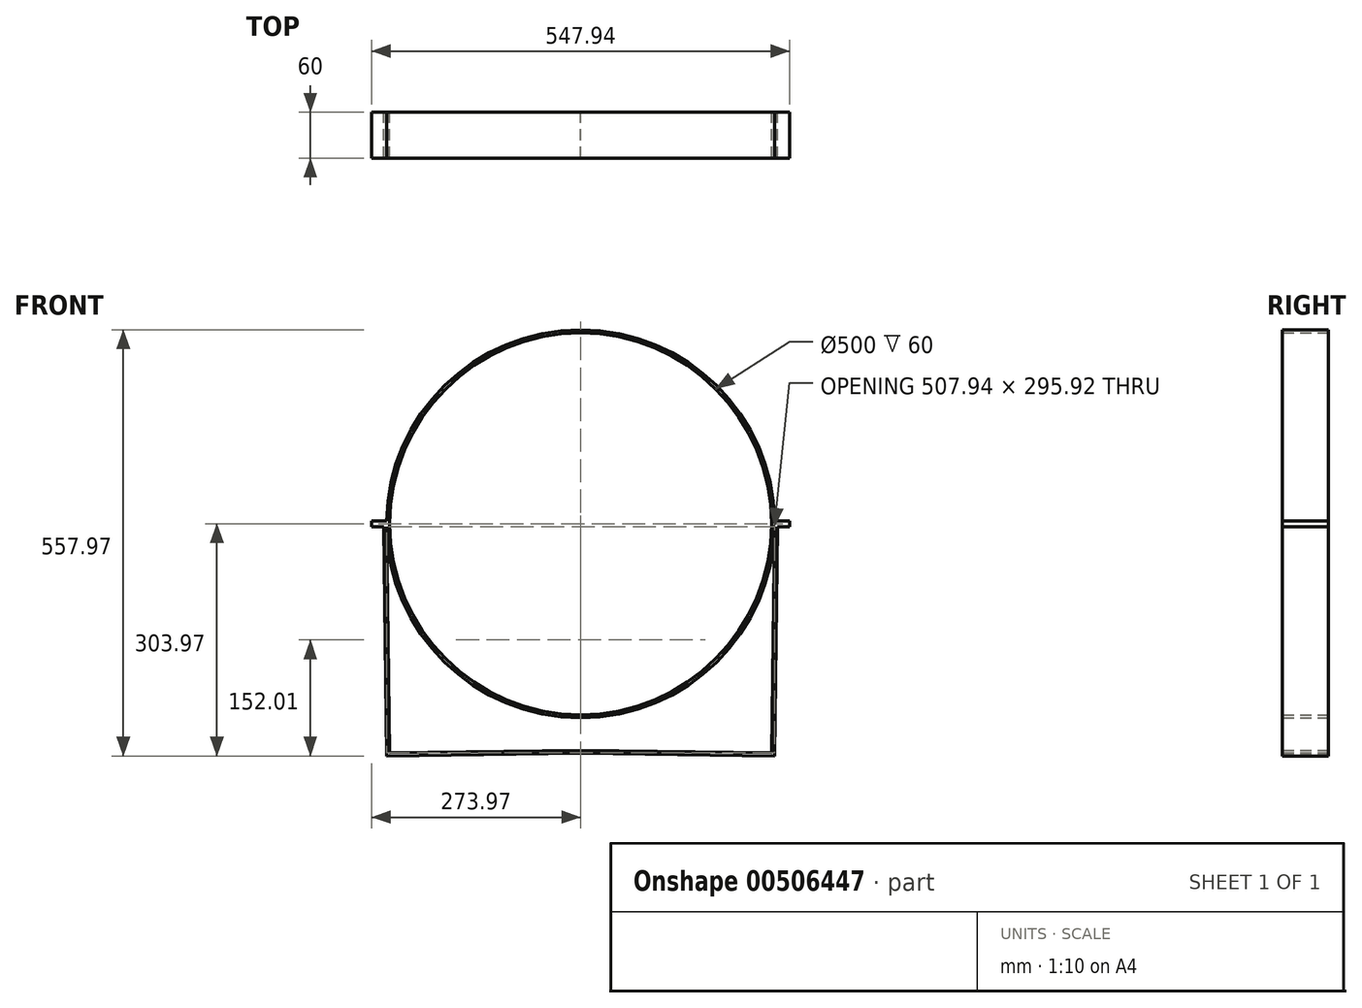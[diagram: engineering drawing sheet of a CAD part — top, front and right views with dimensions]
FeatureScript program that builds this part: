
annotation { "Feature Type Name" : "Feature", "Feature Type Description" : "" }
export const myFeature = defineFeature(function(context is Context, id is Id, definition is map)
    precondition{}
    {
        {
            var Q0;
            Q0=qCreatedBy(makeId("Front.planeOp"),FACE);
            var sketch = newSketch(context, id + "F0", { "sketchPlane" : qUnion([Q0])});
            skCircle(sketch, "E0", {"center": v(0, 0) * mm, "radius": 250 * mm});
            skCircle(sketch, "E1", {"center": v(0, 0) * mm, "radius": 254 * mm});
            skLineSegment(sketch, "E2", {"start": v(0, 0) * mm, "end": v(-690.21, 0) * mm, "construction": true});
            skLineSegment(sketch, "E3", {"start": v(-253.97, 4) * mm, "end": v(-273.97, 4) * mm});
            skLineSegment(sketch, "E4", {"start": v(-273.97, 4) * mm, "end": v(-273.97, 0) * mm});
            skLineSegment(sketch, "E5.MirrorCS", {"start": v(-253.97, -4) * mm, "end": v(-273.97, -4) * mm});
            skLineSegment(sketch, "E6.MirrorCS", {"start": v(-273.97, -4) * mm, "end": v(-273.97, 0) * mm});
            skLineSegment(sketch, "E7", {"start": v(0, 0) * mm, "end": v(0, 668.71) * mm, "construction": true});
            skLineSegment(sketch, "E8.MirrorCS", {"start": v(273.97, 4) * mm, "end": v(273.97, 0) * mm});
            skLineSegment(sketch, "E9.MirrorCS", {"start": v(273.97, -4) * mm, "end": v(273.97, 0) * mm});
            skLineSegment(sketch, "E10.MirrorCS", {"start": v(253.97, 4) * mm, "end": v(273.97, 4) * mm});
            skLineSegment(sketch, "E11.MirrorCS", {"start": v(253.97, -4) * mm, "end": v(273.97, -4) * mm});
            skLineSegment(sketch, "E12", {"start": v(-253.97, -4) * mm, "end": v(-257.97, -4) * mm});
            skLineSegment(sketch, "E13", {"start": v(-257.97, -4) * mm, "end": v(-253.97, -303.97) * mm});
            skLineSegment(sketch, "E14", {"start": v(-253.97, -4) * mm, "end": v(-250.02, -299.92) * mm});
            skLineSegment(sketch, "E15", {"start": v(-250.02, -299.92) * mm, "end": v(0, -296.59) * mm});
            skLineSegment(sketch, "E16", {"start": v(-253.97, -303.97) * mm, "end": v(0, -300.59) * mm});
            skLineSegment(sketch, "E17.MirrorCS", {"start": v(253.97, -4) * mm, "end": v(250.02, -299.92) * mm});
            skLineSegment(sketch, "E18.MirrorCS", {"start": v(257.97, -4) * mm, "end": v(253.97, -303.97) * mm});
            skLineSegment(sketch, "E19.MirrorCS", {"start": v(253.97, -303.97) * mm, "end": v(0, -300.59) * mm});
            skLineSegment(sketch, "E20.MirrorCS", {"start": v(250.02, -299.92) * mm, "end": v(0, -296.59) * mm});
            skSolve(sketch);
        }
        {
            var Q0;
            Q0=qSketchRegion(id+"F0",true);
            extrude(context, id + "F1", {"entities" : qUnion([Q0]), "offsetDistance" : 25 * mm, "depth" : 60 * mm});
        }
    });
